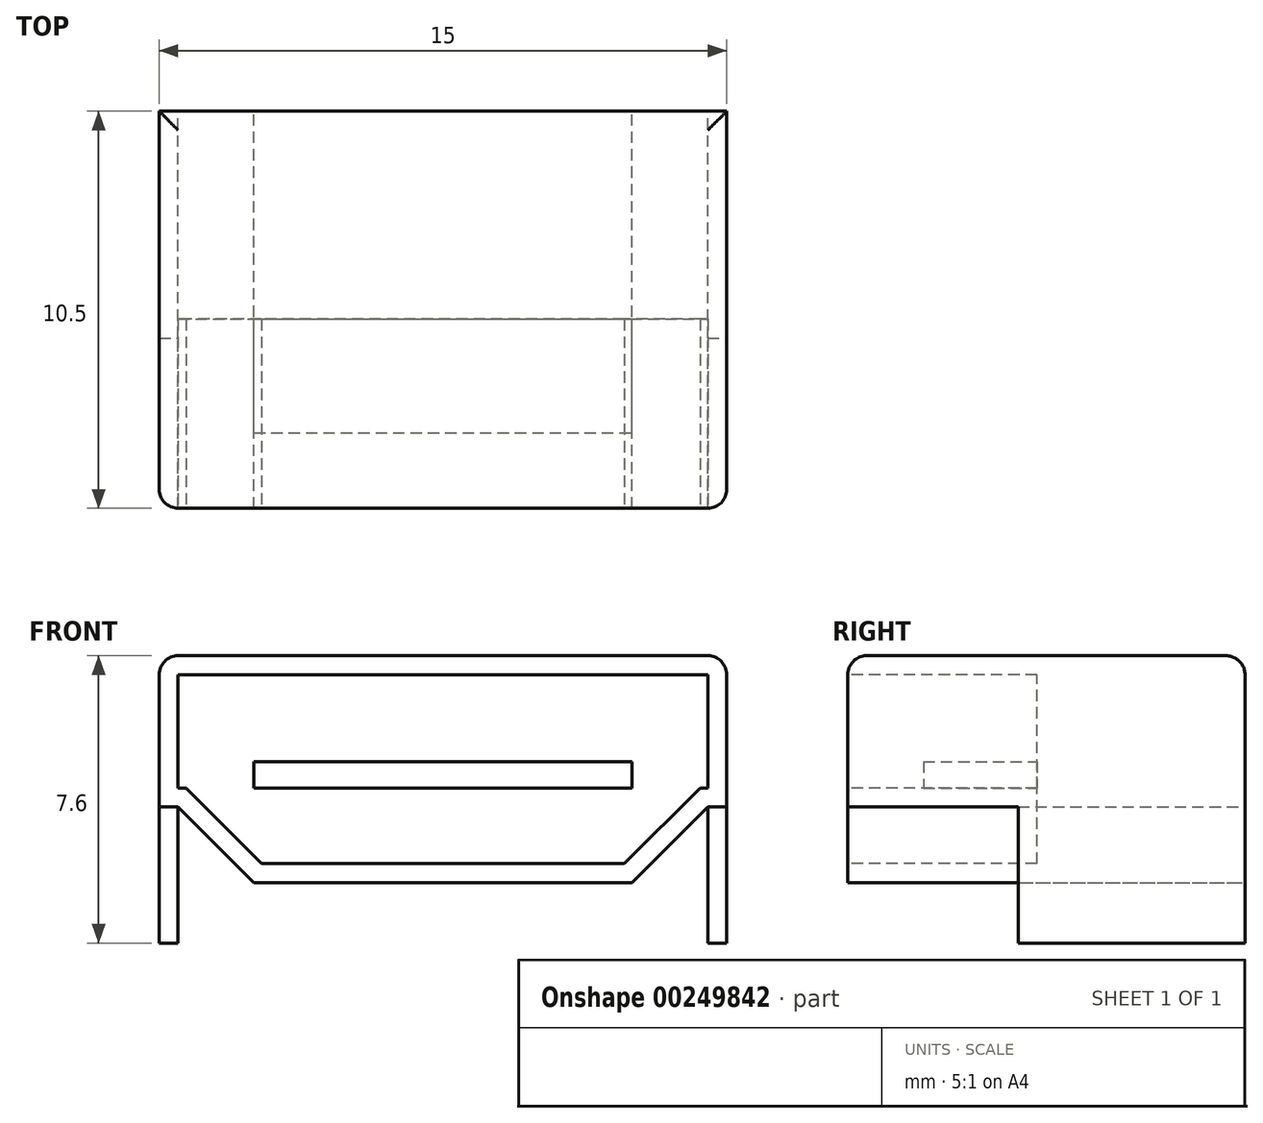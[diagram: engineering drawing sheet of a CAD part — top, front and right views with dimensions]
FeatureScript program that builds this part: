
annotation { "Feature Type Name" : "Feature", "Feature Type Description" : "" }
export const myFeature = defineFeature(function(context is Context, id is Id, definition is map)
    precondition{}
    {
        {
            var Q0;
            Q0=qCreatedBy(makeId("Front.planeOp"),FACE);
            var sketch = newSketch(context, id + "F0", { "sketchPlane" : qUnion([Q0])});
            skLineSegment(sketch, "E0.bottom", {"start": v(0, 0) * mm, "end": v(15, 0) * mm, "construction": true});
            skLineSegment(sketch, "E0.top", {"start": v(0, 6) * mm, "end": v(15, 6) * mm, "construction": true});
            skLineSegment(sketch, "E0.left", {"start": v(0, 0) * mm, "end": v(0, 6) * mm, "construction": true});
            skLineSegment(sketch, "E0.right", {"start": v(15, 0) * mm, "end": v(15, 6) * mm, "construction": true});
            skLineSegment(sketch, "E1", {"start": v(0, 6) * mm, "end": v(15, 6) * mm});
            skLineSegment(sketch, "E2", {"start": v(12.5, 0) * mm, "end": v(2.5, 0) * mm});
            skLineSegment(sketch, "E3", {"start": v(0, 2) * mm, "end": v(0, 6) * mm});
            skLineSegment(sketch, "E4", {"start": v(0, 2) * mm, "end": v(0.5, 2) * mm});
            skLineSegment(sketch, "E5", {"start": v(0.5, 2) * mm, "end": v(2.5, 0) * mm});
            skLineSegment(sketch, "E6", {"start": v(15, 2) * mm, "end": v(15, 2) * mm});
            skLineSegment(sketch, "E7", {"start": v(15, 2) * mm, "end": v(14.5, 2) * mm});
            skLineSegment(sketch, "E8", {"start": v(14.5, 2) * mm, "end": v(12.5, 0) * mm});
            skLineSegment(sketch, "E9", {"start": v(15, 6) * mm, "end": v(15, 2) * mm});
            skSolve(sketch);
        }
        {
            var Q0;
            Q0 = qSketchRegion(id + "F0", true);
            extrude(context, id + "F1", {"entities" : qUnion([Q0]), "depth" : 10.5 * mm});
        }
        {
            var Q0;
            Q0=makeQuery(id+"F1.opExtrude","CAP_FACE",FACE,{"disambiguationData":[OSD([sQuery(id+"F0.wireOp",EDGE,"E1"),sQuery(id+"F0.wireOp",EDGE,"E2"),sQuery(id+"F0.wireOp",EDGE,"E3"),sQuery(id+"F0.wireOp",EDGE,"E4"),sQuery(id+"F0.wireOp",EDGE,"E5"),sQuery(id+"F0.wireOp",EDGE,"E7"),sQuery(id+"F0.wireOp",EDGE,"E8"),sQuery(id+"F0.wireOp",EDGE,"E9")])],"isStart":false});
            var sketch = newSketch(context, id + "F2", { "sketchPlane" : qUnion([Q0])});
            skLineSegment(sketch, "E10", {"start": v(0.5, 5.5) * mm, "end": v(14.5, 5.5) * mm});
            skLineSegment(sketch, "E11", {"start": v(14.5, 5.5) * mm, "end": v(14.5, 2.5) * mm});
            skLineSegment(sketch, "E12", {"start": v(14.5, 2.5) * mm, "end": v(14.3, 2.5) * mm});
            skLineSegment(sketch, "E13", {"start": v(14.3, 2.5) * mm, "end": v(12.3, 0.5) * mm});
            skLineSegment(sketch, "E14", {"start": v(12.3, 0.5) * mm, "end": v(2.7, 0.5) * mm});
            skLineSegment(sketch, "E15", {"start": v(2.7, 0.5) * mm, "end": v(0.7, 2.5) * mm});
            skLineSegment(sketch, "E16", {"start": v(0.7, 2.5) * mm, "end": v(0.5, 2.5) * mm});
            skLineSegment(sketch, "E17", {"start": v(0.5, 2.5) * mm, "end": v(0.5, 5.5) * mm});
            skSolve(sketch);
        }
        {
            var Q0;
            Q0 = qSketchRegion(id + "F2", true);
            extrude(context, id + "F3", {"entities" : qUnion([Q0]), "operationType" : NewBodyOperationType.REMOVE, "oppositeDirection" : true, "depth" : 5 * mm});
        }
        {
            var Q0;
            Q0=makeQuery(id+"F3.boolean.opBoolean","COPY",FACE,{"derivedFrom":makeQuery(id+"F3.opExtrude","CAP_FACE",FACE,{"disambiguationData":[OSD([sQuery(id+"F2.wireOp",EDGE,"E10"),sQuery(id+"F2.wireOp",EDGE,"E11"),sQuery(id+"F2.wireOp",EDGE,"E12"),sQuery(id+"F2.wireOp",EDGE,"E13"),sQuery(id+"F2.wireOp",EDGE,"E14"),sQuery(id+"F2.wireOp",EDGE,"E15"),sQuery(id+"F2.wireOp",EDGE,"E16"),sQuery(id+"F2.wireOp",EDGE,"E17")])],"isStart":false})});
            var sketch = newSketch(context, id + "F4", { "sketchPlane" : qUnion([Q0])});
            skLineSegment(sketch, "E18.bottom", {"start": v(2.5, 3.2) * mm, "end": v(12.5, 3.2) * mm});
            skLineSegment(sketch, "E18.top", {"start": v(2.5, 2.5) * mm, "end": v(12.5, 2.5) * mm});
            skLineSegment(sketch, "E18.left", {"start": v(2.5, 3.2) * mm, "end": v(2.5, 2.5) * mm});
            skLineSegment(sketch, "E18.right", {"start": v(12.5, 3.2) * mm, "end": v(12.5, 2.5) * mm});
            skSolve(sketch);
        }
        {
            var Q0;
            Q0 = qSketchRegion(id + "F4", true);
            extrude(context, id + "F5", {"entities" : qUnion([Q0]), "operationType" : NewBodyOperationType.ADD, "depth" : 3 * mm});
        }
        {
            var Q0;
            Q0=makeQuery(id+"F1.opExtrude","SWEPT_FACE",FACE,{"disambiguationData":[OSD([sQuery(id+"F0.wireOp",EDGE,"E4")])]});
            var sketch = newSketch(context, id + "F6", { "sketchPlane" : qUnion([Q0])});
            skLineSegment(sketch, "E19.bottom", {"start": v(0, 6) * mm, "end": v(0.5, 6) * mm});
            skLineSegment(sketch, "E19.top", {"start": v(0, 0) * mm, "end": v(0.5, 0) * mm});
            skLineSegment(sketch, "E19.left", {"start": v(0, 6) * mm, "end": v(0, 0) * mm});
            skLineSegment(sketch, "E19.right", {"start": v(0.5, 6) * mm, "end": v(0.5, 0) * mm});
            skLineSegment(sketch, "E20.bottom", {"start": v(14.5, 6) * mm, "end": v(15, 6) * mm});
            skLineSegment(sketch, "E20.top", {"start": v(14.5, 0) * mm, "end": v(15, 0) * mm});
            skLineSegment(sketch, "E20.left", {"start": v(14.5, 6) * mm, "end": v(14.5, 0) * mm});
            skLineSegment(sketch, "E20.right", {"start": v(15, 6) * mm, "end": v(15, 0) * mm});
            skSolve(sketch);
        }
        {
            var Q0;
            Q0 = qSketchRegion(id + "F6", true);
            extrude(context, id + "F7", {"entities" : qUnion([Q0]), "operationType" : NewBodyOperationType.ADD, "depth" : 3.6 * mm});
        }
        {
            var Q0;
            Q0=makeQuery(id+"F1.opExtrude","SWEPT_EDGE",EDGE,{"disambiguationData":[OSD([sQuery(id+"F0.wireOp",EDGE,"E1"),sQuery(id+"F0.wireOp",EDGE,"E3")])]});
            var Q1;
            Q1=makeQuery(id+"F1.opExtrude","CAP_EDGE",EDGE,{"disambiguationData":[OSD([sQuery(id+"F0.wireOp",EDGE,"E1")])],"isStart":true});
            var Q2;
            Q2=makeQuery(id+"F1.opExtrude","SWEPT_EDGE",EDGE,{"disambiguationData":[OSD([sQuery(id+"F0.wireOp",EDGE,"E1"),sQuery(id+"F0.wireOp",EDGE,"E9")])]});
            var Q3;
            Q3=makeQuery(id+"F1.opExtrude","CAP_EDGE",EDGE,{"disambiguationData":[OSD([sQuery(id+"F0.wireOp",EDGE,"E1")])],"isStart":false});
            var Q4;
            Q4=makeQuery(id+"F1.opExtrude","CAP_EDGE",EDGE,{"disambiguationData":[OSD([sQuery(id+"F0.wireOp",EDGE,"E3")])],"isStart":false});
            var Q5;
            Q5=makeQuery(id+"F1.opExtrude","CAP_EDGE",EDGE,{"disambiguationData":[OSD([sQuery(id+"F0.wireOp",EDGE,"E9")])],"isStart":false});
            fillet(context, id + "F8", {"entities" : qUnion([Q0, Q1, Q2, Q3, Q4, Q5]), "radius" : 0.5 * mm, "tangentPropagation" : true, "allowEdgeOverflow" : false});
        }
    });
